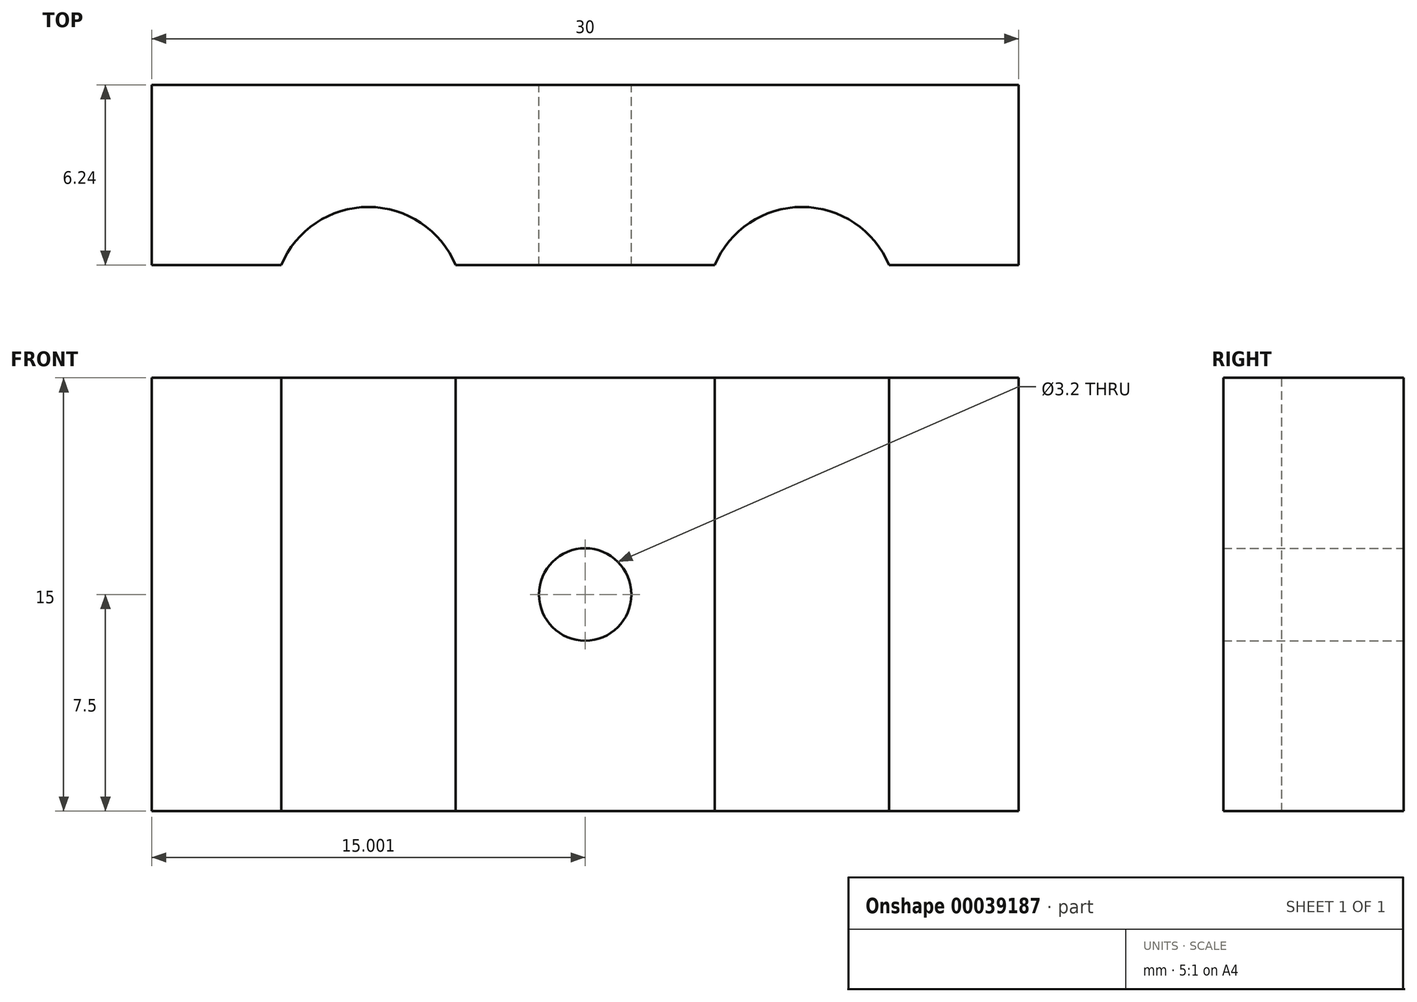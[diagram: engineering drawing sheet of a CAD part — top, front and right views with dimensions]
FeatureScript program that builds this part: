
annotation { "Feature Type Name" : "Feature", "Feature Type Description" : "" }
export const myFeature = defineFeature(function(context is Context, id is Id, definition is map)
    precondition{}
    {
        {
            var Q0;
            Q0=qCreatedBy(makeId("Top.planeOp"),FACE);
            var sketch = newSketch(context, id + "F0", { "sketchPlane" : qUnion([Q0])});
            skLineSegment(sketch, "E0.bottom", {"start": v(-51.93, 20.48) * mm, "end": v(-21.93, 20.48) * mm});
            skLineSegment(sketch, "E0.left", {"start": v(-51.93, 20.48) * mm, "end": v(-51.93, 14.24) * mm});
            skLineSegment(sketch, "E0.right", {"start": v(-21.93, 20.48) * mm, "end": v(-21.93, 12.98) * mm});
            skLineSegment(sketch, "E1", {"start": v(-51.93, 12.98) * mm, "end": v(-21.93, 12.98) * mm, "construction": true});
            skLineSegment(sketch, "E2", {"start": v(-36.93, 20.48) * mm, "end": v(-36.93, 5.48) * mm, "construction": true});
            skArc(sketch, "E3.MirrorC", {"start": v(-32.45, 14.24) * mm, "mid": v(-29.43, 16.25) * mm, "end": v(-26.4, 14.24) * mm});
            skLineSegment(sketch, "E4", {"start": v(-51.93, 14.24) * mm, "end": v(-47.45, 14.24) * mm});
            skLineSegment(sketch, "E5.trimOffspring", {"start": v(-26.4, 14.24) * mm, "end": v(-21.93, 14.24) * mm});
            skLineSegment(sketch, "E6.trimOffspring", {"start": v(-41.4, 14.24) * mm, "end": v(-32.45, 14.24) * mm});
            skArc(sketch, "E7.trimOffspring", {"start": v(-41.4, 14.24) * mm, "mid": v(-44.43, 16.25) * mm, "end": v(-47.45, 14.24) * mm});
            skPoint(sketch, "E8.orphan", {"position": v(-51.93, 5.48) * mm});
            skPoint(sketch, "E9.orphan", {"position": v(-21.93, 5.48) * mm});
            skSolve(sketch);
        }
        {
            var Q0;
            Q0 = qSketchRegion(id + "F0", true);
            extrude(context, id + "F1", {"entities" : qUnion([Q0]), "depth" : 15 * mm});
        }
        {
            var Q0;
            Q0=makeQuery(id+"F1.opExtrude","SWEPT_FACE",FACE,{"disambiguationData":[OSD([sQuery(id+"F0.wireOp",EDGE,"E0.bottom")])]});
            var sketch = newSketch(context, id + "F2", { "sketchPlane" : qUnion([Q0])});
            skLineSegment(sketch, "E10", {"start": v(36.93, 15) * mm, "end": v(36.93, 0) * mm, "construction": true});
            skLineSegment(sketch, "E11", {"start": v(21.93, 7.5) * mm, "end": v(51.93, 7.5) * mm, "construction": true});
            skCircle(sketch, "E12", {"center": v(36.93, 7.5) * mm, "radius": 1.6 * mm});
            skSolve(sketch);
        }
        {
            var Q0;
            Q0=makeQuery(id+"F2.imprint","IMPRINT",FACE,{"disambiguationData":[TD([[makeQuery(id+"F2.imprint","IMPRINT",EDGE,{"derivedFrom":sQuery(id+"F2.wireOp",EDGE,"E12")}),1.0]])]});
            extrude(context, id + "F3", {"entities" : qUnion([Q0]), "operationType" : NewBodyOperationType.REMOVE, "oppositeDirection" : true, "depth" : 7 * mm});
        }
    });
